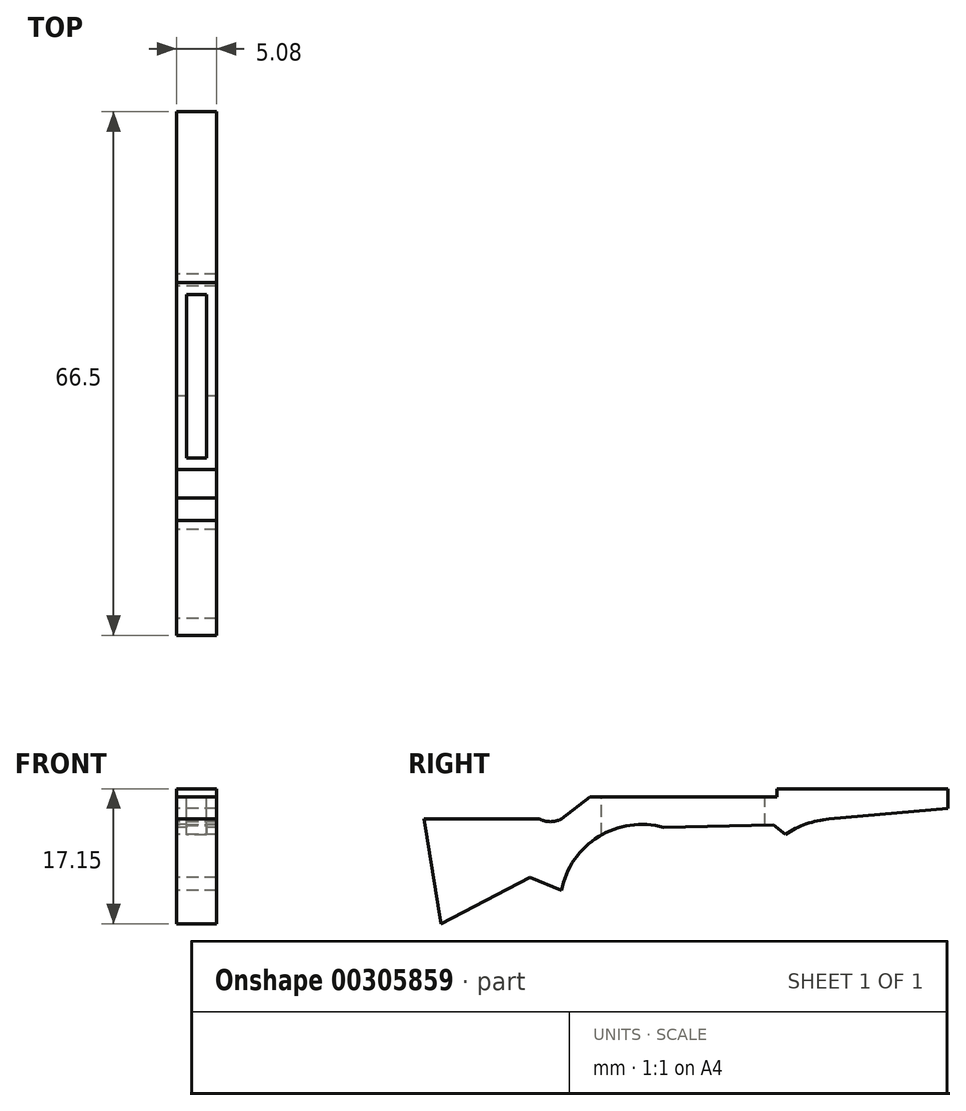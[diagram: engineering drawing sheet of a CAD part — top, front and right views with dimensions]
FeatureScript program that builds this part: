
annotation { "Feature Type Name" : "Feature", "Feature Type Description" : "" }
export const myFeature = defineFeature(function(context is Context, id is Id, definition is map)
    precondition{}
    {
        {
            var Q0;
            Q0=qCreatedBy(makeId("Right.planeOp"),FACE);
            var sketch = newSketch(context, id + "F0", { "sketchPlane" : qUnion([Q0])});
            skLineSegment(sketch, "E0", {"start": v(-58.43, 7.41) * mm, "end": v(-56.3, -5.9) * mm});
            skLineSegment(sketch, "E1", {"start": v(-56.3, -5.9) * mm, "end": v(-44.98, 0) * mm});
            skLineSegment(sketch, "E2", {"start": v(-44.98, 0) * mm, "end": v(-40.97, -1.66) * mm});
            skArc(sketch, "E3", {"start": v(-28.02, 6.34) * mm, "mid": v(-36.25, 5.18) * mm, "end": v(-40.97, -1.66) * mm});
            skLineSegment(sketch, "E4", {"start": v(-58.43, 7.41) * mm, "end": v(-43.83, 7.41) * mm});
            skArc(sketch, "E5", {"start": v(-43.83, 7.41) * mm, "mid": v(-42.4, 7.07) * mm, "end": v(-40.97, 7.41) * mm});
            skLineSegment(sketch, "E6", {"start": v(-40.97, 7.41) * mm, "end": v(-37.4, 10.2) * mm});
            skLineSegment(sketch, "E7", {"start": v(-37.4, 10.2) * mm, "end": v(-13.64, 10.2) * mm});
            skLineSegment(sketch, "E8", {"start": v(-13.64, 10.2) * mm, "end": v(-13.64, 11.25) * mm});
            skLineSegment(sketch, "E9", {"start": v(-13.64, 11.25) * mm, "end": v(8.07, 11.25) * mm});
            skLineSegment(sketch, "E10", {"start": v(8.07, 11.25) * mm, "end": v(8.07, 8.79) * mm});
            skLineSegment(sketch, "E11", {"start": v(8.07, 8.79) * mm, "end": v(-7, 7.41) * mm});
            skArc(sketch, "E12", {"start": v(-7, 7.41) * mm, "mid": v(-9.9, 6.78) * mm, "end": v(-12.57, 5.47) * mm});
            skLineSegment(sketch, "E13", {"start": v(-12.57, 5.47) * mm, "end": v(-14.07, 6.65) * mm});
            skLineSegment(sketch, "E14", {"start": v(-14.07, 6.65) * mm, "end": v(-28.02, 6.34) * mm});
            skSolve(sketch);
        }
        {
            var Q0;
            Q0 = qSketchRegion(id + "F0", true);
            extrude(context, id + "F1", {"entities" : qUnion([Q0]), "endBound" : BoundingType.SYMMETRIC, "depth" : 5.08 * mm});
        }
        {
            var Q0;
            Q0=makeQuery(id+"F1.opExtrude","SWEPT_FACE",FACE,{"disambiguationData":[OSD([sQuery(id+"F0.wireOp",EDGE,"E7")])]});
            var sketch = newSketch(context, id + "F2", { "sketchPlane" : qUnion([Q0])});
            skLineSegment(sketch, "E15.0.0", {"start": v(-2.54, -13.64) * mm, "end": v(-2.54, -37.4) * mm});
            skLineSegment(sketch, "E15.0.1", {"start": v(-2.54, -37.4) * mm, "end": v(2.54, -37.4) * mm});
            skLineSegment(sketch, "E15.0.2", {"start": v(2.54, -37.4) * mm, "end": v(2.54, -13.64) * mm});
            skLineSegment(sketch, "E15.0.3", {"start": v(2.54, -13.64) * mm, "end": v(-2.54, -13.64) * mm});
            skLineSegment(sketch, "E16", {"start": v(0, -13.64) * mm, "end": v(0, -37.4) * mm, "construction": true});
            skLineSegment(sketch, "E17", {"start": v(-2.54, -25.52) * mm, "end": v(0, -25.52) * mm, "construction": true});
            skLineSegment(sketch, "E18", {"start": v(0, -25.52) * mm, "end": v(2.54, -25.52) * mm, "construction": true});
            skLineSegment(sketch, "E19", {"start": v(-1.27, -25.52) * mm, "end": v(-1.27, -35.92) * mm});
            skLineSegment(sketch, "E20", {"start": v(-1.27, -35.92) * mm, "end": v(1.27, -35.92) * mm});
            skPoint(sketch, "E20.endSnap0", {"position": v(1.27, -25.52) * mm});
            skLineSegment(sketch, "E21", {"start": v(1.27, -35.92) * mm, "end": v(1.27, -25.52) * mm});
            skLineSegment(sketch, "E22", {"start": v(1.27, -25.52) * mm, "end": v(1.27, -15.17) * mm});
            skLineSegment(sketch, "E23", {"start": v(1.27, -15.17) * mm, "end": v(-1.27, -15.17) * mm});
            skLineSegment(sketch, "E24", {"start": v(-1.27, -15.17) * mm, "end": v(-1.27, -25.52) * mm});
            skSolve(sketch);
        }
        {
            var Q0;
            Q0=makeQuery(id+"F2.imprint","IMPRINT",FACE,{"disambiguationData":[TD([[makeQuery(id+"F2.imprint","IMPRINT",EDGE,{"derivedFrom":sQuery(id+"F2.wireOp",EDGE,"E19")}),1.0]])]});
            extrude(context, id + "F3", {"entities" : qUnion([Q0]), "operationType" : NewBodyOperationType.REMOVE, "oppositeDirection" : true, "depth" : 25.4 * mm});
        }
    });
